# Revit family: ES10120BA
name_source: partatom
category: Furniture
units: mm (PartAtom-declared; Revit-internal decimal feet)

## family parameters
Always vertical = Yes
Cut with Voids When Loaded = No
OmniClass Number = 23.40.20.00
OmniClass Title = General Furniture and Specialties
Room Calculation Point = No
Shared = No
Work Plane-Based = No

## types (4) — shared parameters
Depth = 225 mm  [stored 0.738189 ft]
Description = Round polyethylene base. The inner counterweight is included.
Height = 430 mm
Manufacturer = Sandler
Model = ES10120BA + ES20040TP-Wood
URL = https://www.sandlerseating.com
Width = 225 mm  [stored 0.738189 ft]
zero-valued in all types: Default Elevation

## per-type parameters (varying)
| type | Table Top |
| ES10120BA + Round 40cm Wood Top | IC_EsOcc_TT_Rnd_Wood : IC_TT_Rnd Wood 40 diameter |
| ES10120BA + Round 50cm Wood Top | IC_EsOcc_TT_Rnd_Wood : IC_TT_Rnd Wood 50 diameter |
| ES10120BA + Round 40cm HPL Top | IC_EsOcc_TT_Rnd_HPL : IC_TT_Rnd_HPL 40 diameter |
| ES10120BA + Round 50cm HPL Top | IC_EsOcc_TT_Rnd_HPL : IC_TT_Rnd_HPL 50 diameter |

note: [stored X ft] marks values corroborated as IEEE doubles in the binary element streams (Revit-internal decimal feet)

## geometry (parser evidence)
native form markers: Sweep x6
no freeform markers — native parametric forms only
